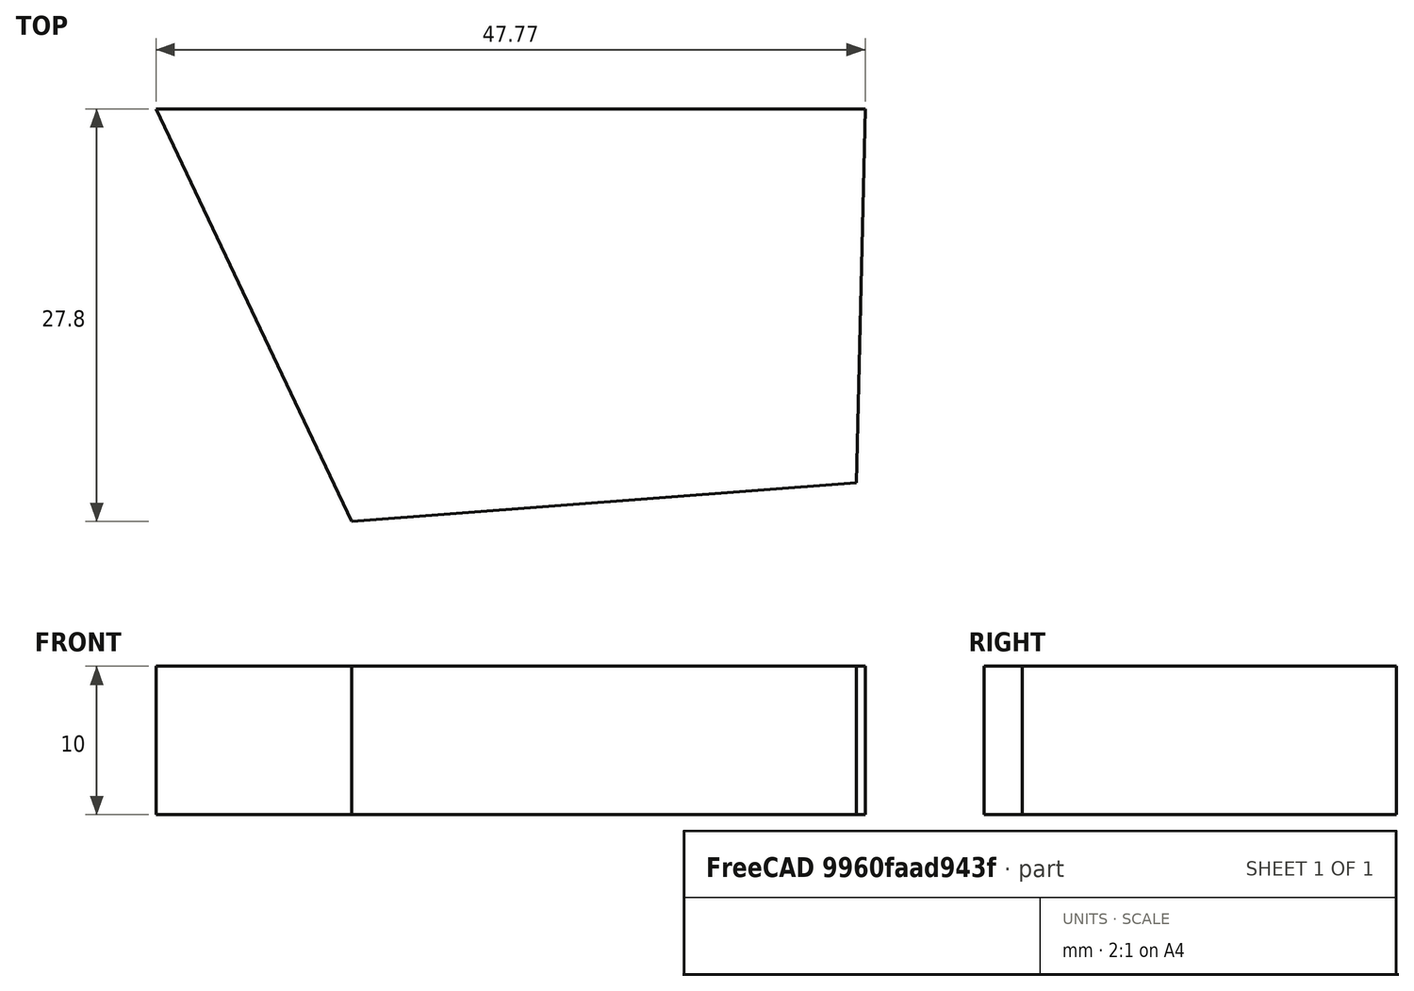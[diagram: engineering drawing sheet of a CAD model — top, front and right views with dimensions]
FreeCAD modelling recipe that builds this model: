
FCSTD DOCUMENT  (FreeCAD 1.0R38806 (Git))
Label: multilinea
License: All rights reserved
LicenseURL: https://en.wikipedia.org/wiki/All_rights_reserved
objects: Sketcher::SketchObject×1, Part::Extrusion×1
note: 3 computed .brp shape members not serialized (recipe doc carries the construction recipe); baked Part::Feature solids carry a one-line shape summary decoded from their .brp

FEATURE [Sketcher::SketchObject] Sketch
  ArcFitTolerance = 1e-06
  FullyConstrained = false
  MakeInternals = false
  sketch-geometry (4):
    g0: LineSegment StartX=33.6678 StartY=39.0633 StartZ=0 EndX=66.3232 EndY=44.1399 EndZ=0
    g1: LineSegment StartX=66.3232 StartY=44.1399 StartZ=0 EndX=67.1031 EndY=11.1014 EndZ=0
    g2: LineSegment StartX=67.1031 StartY=11.1014 StartZ=0 EndX=34.4476 EndY=6.02485 EndZ=0
    g3: LineSegment StartX=34.4476 StartY=6.02485 StartZ=0 EndX=33.6678 EndY=39.0633 EndZ=0
  constraints (7):
    c: Coincident(g0,g1)
    c: Coincident(g1,g2)
    c: Coincident(g2,g3)
    c: Coincident(g3,g0)
    c: Equal(g0,g1)
    c: Equal(g1,g2)
    c: Equal(g2,g3)
FEATURE [Part::Extrusion] Extrude  label="rectagulo"
  Base = -> Sketch
  Dir = (0,0,1)
  DirMode = 2
  FaceMakerClass = Part::FaceMakerBullseye
  FaceMakerMode = 3
  LengthFwd = 10
  LengthRev = 0
  Solid = true
  Symmetric = false
